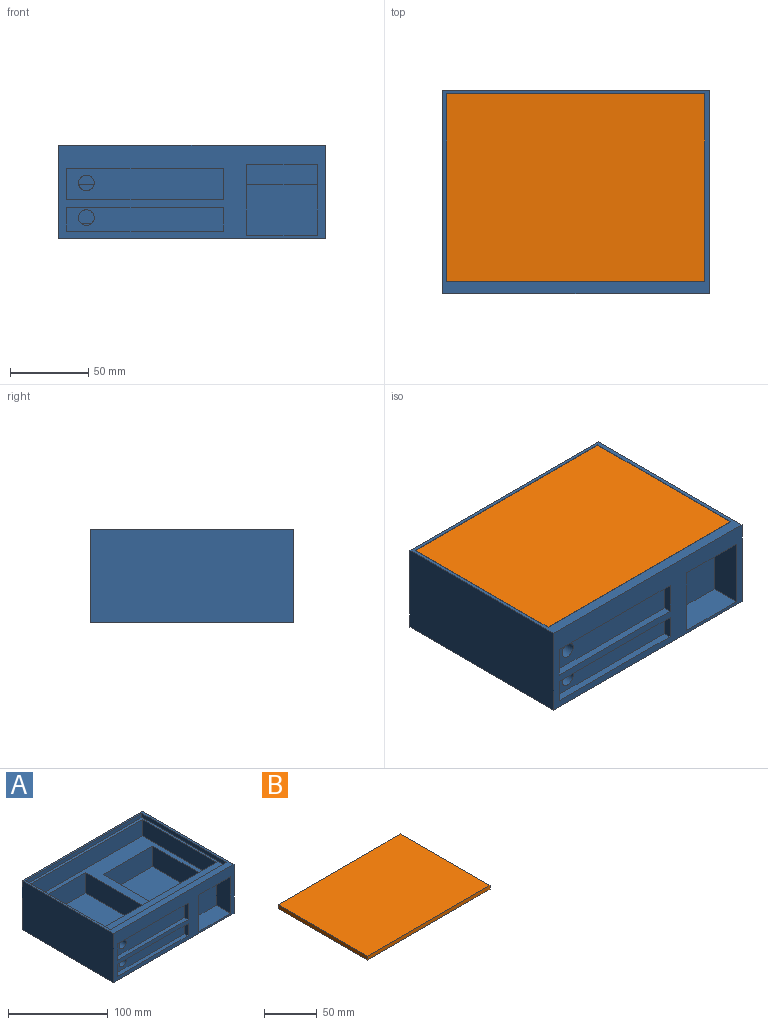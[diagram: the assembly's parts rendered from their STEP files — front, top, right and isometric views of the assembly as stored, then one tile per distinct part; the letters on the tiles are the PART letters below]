
ASSEMBLY  parts=2 mates=1
PART A: 43 faces, bbox 170x130x60 mm
  f0: plane 160x20mm, normal (0,1,0), area 2593.7mm2, adj f2,f4,f5,f12,f13,f35,f38
  f1: plane 170x130mm, normal (0,0,1), area 2300mm2, adj f6,f7,f9,f10,f39,f40,f41,f42
  f2: plane 125x52.57mm, normal (-1,0,0), area 3000mm2, adj f0,f3,f5,f6,f11,f12,f14,f38
  f3: plane 160x20mm, normal (0,-1,0), area 3200mm2, adj f2,f4,f5,f38
  f4: plane 105x20mm, normal (1,0,0), area 2100mm2, adj f0,f3,f5,f38
  f5: plane 160x105mm, normal (0,0,1), area 4500.6mm2, adj f0,f2,f3,f4,f14,f25,f26,f27
  f6: plane 170x60mm, normal (0,-1,0), area 4675mm2, adj f1,f2,f7,f8,f9,f11,f12,f13
  f7: plane 130x60mm, normal (-1,0,0), area 7800mm2, adj f1,f6,f8,f10
  f8: plane 170x130mm, normal (0,0,-1), area 22100mm2, adj f6,f7,f9,f10
  f9: plane 130x60mm, normal (1,0,0), area 7800mm2, adj f1,f6,f8,f10
  f10: plane 170x60mm, normal (0,1,0), area 10200mm2, adj f1,f7,f8,f9
  f11: plane 45x20mm, normal (0,0,1), area 900mm2, adj f2,f6,f13,f14
  f12: plane 45x20mm, normal (0,0,-1), area 900mm2, adj f0,f2,f6,f13
  f13: plane 45x20mm, normal (1,0,0), area 900mm2, adj f0,f6,f11,f12,f14
  f14: plane 45x32.57mm, normal (0,-1,0), area 1465.8mm2, adj f2,f5,f11,f13
  f15: plane 100x5mm, normal (0,0,-1), area 500mm2, adj f6,f16,f18,f19
  f16: plane 20x5mm, normal (1,0,0), area 100mm2, adj f6,f15,f17,f19
  f17: plane 100x5mm, normal (0,0,1), area 500mm2, adj f6,f16,f18,f19
  f18: plane 20x5mm, normal (-1,0,0), area 100mm2, adj f6,f15,f17,f19
  f19: plane 100x20mm, normal (0,-1,0), area 1921.5mm2, adj f15,f16,f17,f18,f35
  f20: plane 15x5mm, normal (1,0,0), area 75mm2, adj f6,f21,f23,f24
  f21: plane 100x5mm, normal (0,0,1), area 500mm2, adj f6,f20,f22,f24
  f22: plane 15x5mm, normal (-1,0,0), area 75mm2, adj f6,f21,f23,f24
  f23: plane 100x5mm, normal (0,0,-1), area 500mm2, adj f6,f20,f22,f24
  f24: plane 100x15mm, normal (0,-1,0), area 1421.5mm2, adj f20,f21,f22,f23,f36
  f25: plane 70x25mm, normal (0,-1,0), area 1750mm2, adj f5,f26,f28,f29
  f26: plane 95x25mm, normal (1,0,0), area 2375mm2, adj f5,f25,f27,f29
  f27: plane 70x25mm, normal (0,1,0), area 1646.1mm2, adj f5,f26,f28,f29,f35,f36
  f28: plane 95x25mm, normal (-1,0,0), area 2375mm2, adj f5,f25,f27,f29
  f29: plane 95x70mm, normal (0,0,1), area 6650mm2, adj f25,f26,f27,f28,f37
  f30: plane 70x25mm, normal (0,-1,0), area 1750mm2, adj f5,f31,f33,f34
  f31: plane 80x25mm, normal (1,0,0), area 2000mm2, adj f5,f30,f32,f34
  f32: plane 70x25mm, normal (0,1,0), area 1750mm2, adj f5,f31,f33,f34
  f33: plane 80x25mm, normal (-1,0,0), area 2000mm2, adj f5,f30,f32,f34
  f34: plane 80x70mm, normal (0,0,1), area 5600mm2, adj f30,f31,f32,f33
  f35: cylinder r=5mm len=20mm, axis (0,-1,0), area 541.9mm2, adj f0,f5,f19,f27
  f36: cylinder r=5mm len=20mm, axis (0,-1,0), area 628.3mm2, adj f24,f27,f37
  f37: plane 6.76x1.32mm, normal (0,-1,0), area 6.1mm2, adj f29,f36
  f38: plane 165x120mm, normal (0,0,1), area 3000mm2, adj f0,f2,f3,f4,f39,f40,f41,f42
  f39: plane 165x5mm, normal (0,-1,0), area 825mm2, adj f1,f38,f40,f42
  f40: plane 120x5mm, normal (1,0,0), area 600mm2, adj f1,f38,f39,f41
  f41: plane 165x5mm, normal (0,1,0), area 825mm2, adj f1,f38,f40,f42
  f42: plane 120x5mm, normal (-1,0,0), area 600mm2, adj f1,f38,f39,f41
PART B: 6 faces, bbox 165x120x4.5 mm
  f0: plane 165x4.5mm, normal (0,1,0), area 742.5mm2, adj f1,f3,f4,f5
  f1: plane 120x4.5mm, normal (-1,0,0), area 540mm2, adj f0,f2,f4,f5
  f2: plane 165x4.5mm, normal (0,-1,0), area 742.5mm2, adj f1,f3,f4,f5
  f3: plane 120x4.5mm, normal (1,0,0), area 540mm2, adj f0,f2,f4,f5
  f4: plane 165x120mm, normal (0,0,1), area 19800mm2, adj f0,f1,f2,f3
  f5: plane 165x120mm, normal (0,0,-1), area 19800mm2, adj f0,f1,f2,f3
PLACE A t=(1.85,-51.54,13.16)mm
PLACE B t=(1.77,16.15,43.41)mm
MATE fastened B.f1 <-> A.f40  axis (-1,0,0) through (-80.73,16.15,45.66)mm
